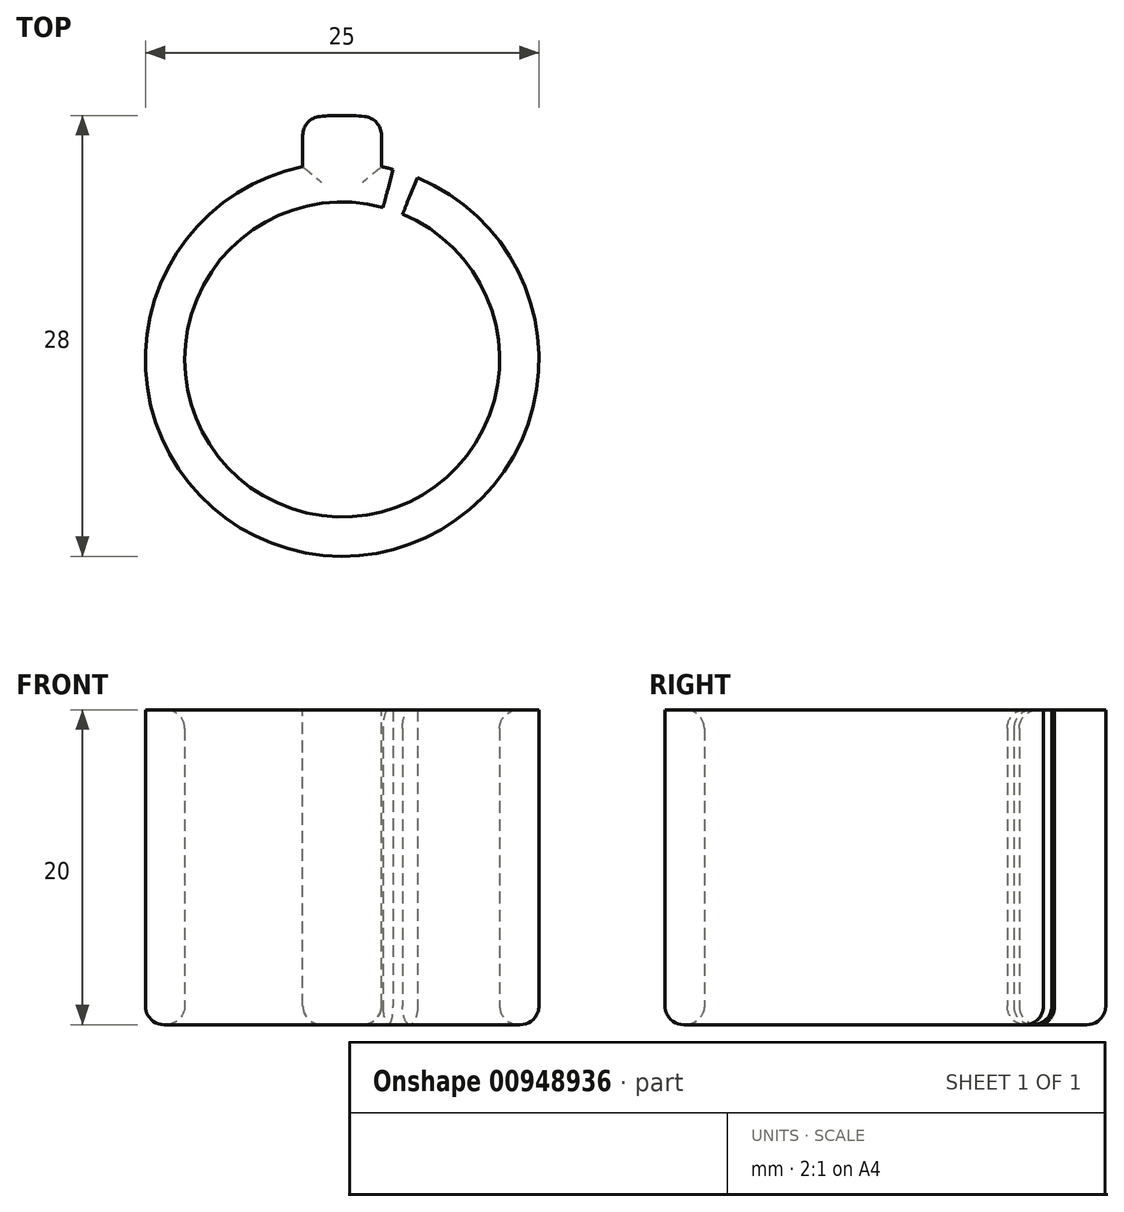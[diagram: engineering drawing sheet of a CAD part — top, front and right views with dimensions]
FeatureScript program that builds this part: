
annotation { "Feature Type Name" : "Feature", "Feature Type Description" : "" }
export const myFeature = defineFeature(function(context is Context, id is Id, definition is map)
    precondition{}
    {
        {
            var Q0;
            Q0=qCreatedBy(makeId("Top.planeOp"),FACE);
            var sketch = newSketch(context, id + "F0", { "sketchPlane" : qUnion([Q0])});
            skCircle(sketch, "E0", {"center": v(0, 0) * mm, "radius": 10 * mm});
            skCircle(sketch, "E1.0", {"center": v(0, 0) * mm, "radius": 12.5 * mm});
            skSolve(sketch);
        }
        {
            var Q0;
            Q0 = qSketchRegion(id + "F0", true);
            extrude(context, id + "F1", {"entities" : qUnion([Q0]), "depth" : 20 * mm, "offsetDistance" : 25 * mm});
        }
        {
            var Q0;
            Q0=makeQuery(id+"F1.opExtrude","CAP_FACE",FACE,{"disambiguationData":[OSD([sQuery(id+"F0.wireOp",EDGE,"E0"),sQuery(id+"F0.wireOp",EDGE,"E1.0")])],"isStart":false});
            var sketch = newSketch(context, id + "F2", { "sketchPlane" : qUnion([Q0])});
            skArc(sketch, "E2", {"start": v(2.5, 15.3) * mm, "mid": v(0, 15.5) * mm, "end": v(-2.5, 15.3) * mm});
            skLineSegment(sketch, "E3.left", {"start": v(2.5, 12.25) * mm, "end": v(2.5, 15.3) * mm});
            skLineSegment(sketch, "E3.right", {"start": v(-2.5, 12.25) * mm, "end": v(-2.5, 15.3) * mm});
            skPoint(sketch, "E3.middle", {"position": v(0, 11.22) * mm});
            skArc(sketch, "E4.0", {"start": v(2.5, 12.25) * mm, "mid": v(0, 12.5) * mm, "end": v(-2.5, 12.25) * mm});
            skPoint(sketch, "E3.bottom.end.orphan", {"position": v(-2.5, 3.8) * mm});
            skPoint(sketch, "E3.bottom.start.orphan", {"position": v(2.5, 3.8) * mm});
            skPoint(sketch, "E3.top.end.orphan", {"position": v(-2.5, 18.63) * mm});
            skPoint(sketch, "E3.top.start.orphan", {"position": v(2.5, 18.63) * mm});
            skSolve(sketch);
        }
        {
            var Q0;
            Q0 = qSketchRegion(id + "F2", true);
            var Q1;
            Q1=makeQuery(id+"F1.opExtrude","CAP_FACE",FACE,{"disambiguationData":[OSD([sQuery(id+"F0.wireOp",EDGE,"E0"),sQuery(id+"F0.wireOp",EDGE,"E1.0")])],"isStart":true});
            extrude(context, id + "F3", {"entities" : qUnion([Q0]), "operationType" : NewBodyOperationType.ADD, "endBound" : BoundingType.UP_TO_SURFACE, "oppositeDirection" : true, "depth" : 25 * mm, "endBoundEntityFace" : qUnion([Q1]), "offsetDistance" : 25 * mm});
        }
        {
            var Q0;
            Q0=makeQuery(id+"F3.opExtrude","SWEPT_EDGE",EDGE,{"disambiguationData":[OSD([sQuery(id+"F0.wireOp",EDGE,"E1.0"),sQuery(id+"F2.wireOp",EDGE,"E3.right"),sQuery(id+"F2.wireOp",EDGE,"E4.0")])]});
            var Q1;
            Q1=makeQuery(id+"F3.opExtrude","SWEPT_EDGE",EDGE,{"disambiguationData":[OSD([sQuery(id+"F2.wireOp",EDGE,"E2"),sQuery(id+"F2.wireOp",EDGE,"E3.right")])]});
            var Q2;
            Q2=makeQuery(id+"F3.opExtrude","SWEPT_EDGE",EDGE,{"disambiguationData":[OSD([sQuery(id+"F2.wireOp",EDGE,"E2"),sQuery(id+"F2.wireOp",EDGE,"E3.left")])]});
            var Q3;
            Q3=makeQuery(id+"F3.opExtrude","SWEPT_EDGE",EDGE,{"disambiguationData":[OSD([sQuery(id+"F0.wireOp",EDGE,"E1.0"),sQuery(id+"F2.wireOp",EDGE,"E3.left"),sQuery(id+"F2.wireOp",EDGE,"E4.0")])]});
            fillet(context, id + "F4", {"entities" : qUnion([Q0, Q1, Q2, Q3]), "tangentPropagation" : true, "radius" : 1.2 * mm, "defaultsChanged" : false, "vertexSettings" : [], "allowEdgeOverflow" : false});
        }
        {
            var Q0;
            Q0=qCreatedBy(makeId("Right.planeOp"),FACE);
            var sketch = newSketch(context, id + "F5", { "sketchPlane" : qUnion([Q0])});
            skLineSegment(sketch, "E5", {"start": v(0, -27.14) * mm, "end": v(0, 60.14) * mm, "construction": true});
            skSolve(sketch);
        }
        {
            var Q0;
            Q0=makeQuery(id+"F1.opExtrude","CAP_EDGE",EDGE,{"disambiguationData":[OSD([sQuery(id+"F0.wireOp",EDGE,"E0")])],"isStart":false});
            var Q1;
            Q1=makeQuery(id+"FP30VpP1jHtccPG_1.1.F3.opExtrude","CAP_EDGE",EDGE,{"disambiguationData":[OSD([sQuery(id+"F2.wireOp",EDGE,"E2")])],"isStart":true});
            var Q2;
            {var subQ0=sQuery(id+"F2.wireOp",EDGE,"E4.0");var subQ1=sQuery(id+"F2.wireOp",EDGE,"E3.right");var subQ2=sQuery(id+"F2.wireOp",EDGE,"E3.left");var subQ3=sQuery(id+"F2.wireOp",EDGE,"E2");Q2=makeQuery(id+"FP30VpP1jHtccPG_1.9.F3.boolean.opBoolean","MERGE",FACE,{"derivedFrom":[makeQuery(id+"FP30VpP1jHtccPG_1.8.F3.boolean.opBoolean","MERGE",FACE,{"derivedFrom":[makeQuery(id+"FP30VpP1jHtccPG_1.7.F3.boolean.opBoolean","MERGE",FACE,{"derivedFrom":[makeQuery(id+"FP30VpP1jHtccPG_1.6.F3.boolean.opBoolean","MERGE",FACE,{"derivedFrom":[makeQuery(id+"FP30VpP1jHtccPG_1.5.F3.boolean.opBoolean","MERGE",FACE,{"derivedFrom":[makeQuery(id+"FP30VpP1jHtccPG_1.4.F3.boolean.opBoolean","MERGE",FACE,{"derivedFrom":[makeQuery(id+"FP30VpP1jHtccPG_1.3.F3.boolean.opBoolean","MERGE",FACE,{"derivedFrom":[makeQuery(id+"FP30VpP1jHtccPG_1.2.F3.boolean.opBoolean","MERGE",FACE,{"derivedFrom":[makeQuery(id+"FP30VpP1jHtccPG_1.1.F3.boolean.opBoolean","MERGE",FACE,{"derivedFrom":[makeQuery(id+"F3.boolean.opBoolean","MERGE",FACE,{"derivedFrom":[makeQuery(id+"F1.opExtrude","CAP_FACE",FACE,{"disambiguationData":[OSD([sQuery(id+"F0.wireOp",EDGE,"E0"),sQuery(id+"F0.wireOp",EDGE,"E1.0")])],"isStart":true}),makeQuery(id+"F3.opExtrude","CAP_FACE",FACE,{"disambiguationData":[OSD([subQ3,subQ2,subQ1,subQ0])],"isStart":false})]}),makeQuery(id+"FP30VpP1jHtccPG_1.1.F3.opExtrude","CAP_FACE",FACE,{"disambiguationData":[OSD([subQ3,subQ2,subQ1,subQ0])],"isStart":false})]}),makeQuery(id+"FP30VpP1jHtccPG_1.2.F3.opExtrude","CAP_FACE",FACE,{"disambiguationData":[OSD([subQ3,subQ2,subQ1,subQ0])],"isStart":false})]}),makeQuery(id+"FP30VpP1jHtccPG_1.3.F3.opExtrude","CAP_FACE",FACE,{"disambiguationData":[OSD([subQ3,subQ2,subQ1,subQ0])],"isStart":false})]}),makeQuery(id+"FP30VpP1jHtccPG_1.4.F3.opExtrude","CAP_FACE",FACE,{"disambiguationData":[OSD([subQ3,subQ2,subQ1,subQ0])],"isStart":false})]}),makeQuery(id+"FP30VpP1jHtccPG_1.5.F3.opExtrude","CAP_FACE",FACE,{"disambiguationData":[OSD([subQ3,subQ2,subQ1,subQ0])],"isStart":false})]}),makeQuery(id+"FP30VpP1jHtccPG_1.6.F3.opExtrude","CAP_FACE",FACE,{"disambiguationData":[OSD([subQ3,subQ2,subQ1,subQ0])],"isStart":false})]}),makeQuery(id+"FP30VpP1jHtccPG_1.7.F3.opExtrude","CAP_FACE",FACE,{"disambiguationData":[OSD([subQ3,subQ2,subQ1,subQ0])],"isStart":false})]}),makeQuery(id+"FP30VpP1jHtccPG_1.8.F3.opExtrude","CAP_FACE",FACE,{"disambiguationData":[OSD([subQ3,subQ2,subQ1,subQ0])],"isStart":false})]}),makeQuery(id+"FP30VpP1jHtccPG_1.9.F3.opExtrude","CAP_FACE",FACE,{"disambiguationData":[OSD([subQ3,subQ2,subQ1,subQ0])],"isStart":false})]});}
            fillet(context, id + "F6", {"entities" : qUnion([Q0, Q1, Q2]), "tangentPropagation" : true, "radius" : 1.2 * mm, "defaultsChanged" : false, "vertexSettings" : [], "allowEdgeOverflow" : false});
        }
        {
            var Q0;
            {var subQ0=sQuery(id+"F2.wireOp",EDGE,"E4.0");var subQ1=sQuery(id+"F2.wireOp",EDGE,"E3.right");var subQ2=sQuery(id+"F2.wireOp",EDGE,"E3.left");var subQ3=sQuery(id+"F2.wireOp",EDGE,"E2");Q0=makeQuery(id+"FP30VpP1jHtccPG_1.9.F3.boolean.opBoolean","MERGE",FACE,{"derivedFrom":[makeQuery(id+"FP30VpP1jHtccPG_1.8.F3.boolean.opBoolean","MERGE",FACE,{"derivedFrom":[makeQuery(id+"FP30VpP1jHtccPG_1.7.F3.boolean.opBoolean","MERGE",FACE,{"derivedFrom":[makeQuery(id+"FP30VpP1jHtccPG_1.6.F3.boolean.opBoolean","MERGE",FACE,{"derivedFrom":[makeQuery(id+"FP30VpP1jHtccPG_1.5.F3.boolean.opBoolean","MERGE",FACE,{"derivedFrom":[makeQuery(id+"FP30VpP1jHtccPG_1.4.F3.boolean.opBoolean","MERGE",FACE,{"derivedFrom":[makeQuery(id+"FP30VpP1jHtccPG_1.3.F3.boolean.opBoolean","MERGE",FACE,{"derivedFrom":[makeQuery(id+"FP30VpP1jHtccPG_1.2.F3.boolean.opBoolean","MERGE",FACE,{"derivedFrom":[makeQuery(id+"FP30VpP1jHtccPG_1.1.F3.boolean.opBoolean","MERGE",FACE,{"derivedFrom":[makeQuery(id+"F3.boolean.opBoolean","MERGE",FACE,{"derivedFrom":[makeQuery(id+"F1.opExtrude","CAP_FACE",FACE,{"disambiguationData":[OSD([sQuery(id+"F0.wireOp",EDGE,"E0"),sQuery(id+"F0.wireOp",EDGE,"E1.0")])],"isStart":false}),makeQuery(id+"F3.opExtrude","CAP_FACE",FACE,{"disambiguationData":[OSD([subQ3,subQ2,subQ1,subQ0])],"isStart":true})]}),makeQuery(id+"FP30VpP1jHtccPG_1.1.F3.opExtrude","CAP_FACE",FACE,{"disambiguationData":[OSD([subQ3,subQ2,subQ1,subQ0])],"isStart":true})]}),makeQuery(id+"FP30VpP1jHtccPG_1.2.F3.opExtrude","CAP_FACE",FACE,{"disambiguationData":[OSD([subQ3,subQ2,subQ1,subQ0])],"isStart":true})]}),makeQuery(id+"FP30VpP1jHtccPG_1.3.F3.opExtrude","CAP_FACE",FACE,{"disambiguationData":[OSD([subQ3,subQ2,subQ1,subQ0])],"isStart":true})]}),makeQuery(id+"FP30VpP1jHtccPG_1.4.F3.opExtrude","CAP_FACE",FACE,{"disambiguationData":[OSD([subQ3,subQ2,subQ1,subQ0])],"isStart":true})]}),makeQuery(id+"FP30VpP1jHtccPG_1.5.F3.opExtrude","CAP_FACE",FACE,{"disambiguationData":[OSD([subQ3,subQ2,subQ1,subQ0])],"isStart":true})]}),makeQuery(id+"FP30VpP1jHtccPG_1.6.F3.opExtrude","CAP_FACE",FACE,{"disambiguationData":[OSD([subQ3,subQ2,subQ1,subQ0])],"isStart":true})]}),makeQuery(id+"FP30VpP1jHtccPG_1.7.F3.opExtrude","CAP_FACE",FACE,{"disambiguationData":[OSD([subQ3,subQ2,subQ1,subQ0])],"isStart":true})]}),makeQuery(id+"FP30VpP1jHtccPG_1.8.F3.opExtrude","CAP_FACE",FACE,{"disambiguationData":[OSD([subQ3,subQ2,subQ1,subQ0])],"isStart":true})]}),makeQuery(id+"FP30VpP1jHtccPG_1.9.F3.opExtrude","CAP_FACE",FACE,{"disambiguationData":[OSD([subQ3,subQ2,subQ1,subQ0])],"isStart":true})]});}
            var sketch = newSketch(context, id + "F7", { "sketchPlane" : qUnion([Q0])});
            skLineSegment(sketch, "E6", {"start": v(0, 0) * mm, "end": v(8.08, 30.08) * mm});
            skLineSegment(sketch, "E7", {"start": v(8.08, 30.08) * mm, "end": v(11.44, 27.58) * mm});
            skLineSegment(sketch, "E8", {"start": v(11.44, 27.58) * mm, "end": v(0, 0) * mm});
            skSolve(sketch);
        }
        {
            var Q0;
            Q0 = qSketchRegion(id + "F7", true);
            extrude(context, id + "F8", {"entities" : qUnion([Q0]), "operationType" : NewBodyOperationType.REMOVE, "endBound" : BoundingType.THROUGH_ALL, "oppositeDirection" : true, "depth" : 25 * mm, "offsetDistance" : 25 * mm});
        }
    });
